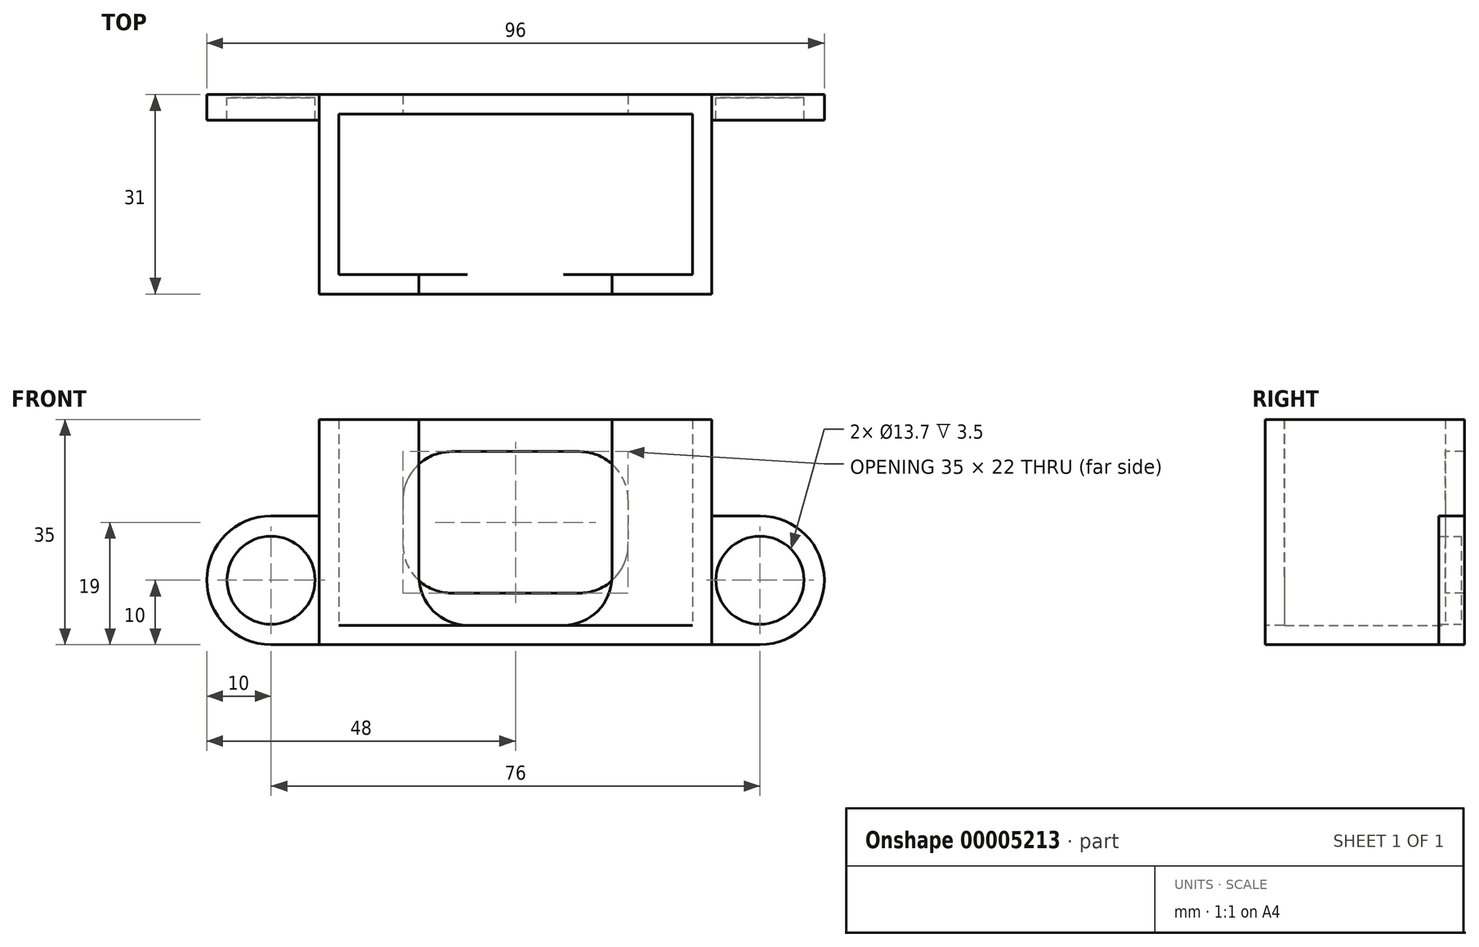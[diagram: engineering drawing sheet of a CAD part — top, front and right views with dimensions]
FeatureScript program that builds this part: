
annotation { "Feature Type Name" : "Feature", "Feature Type Description" : "" }
export const myFeature = defineFeature(function(context is Context, id is Id, definition is map)
    precondition{}
    {
        {
            var Q0;
            Q0=qCreatedBy(makeId("Top.planeOp"),FACE);
            var sketch = newSketch(context, id + "F0", { "sketchPlane" : qUnion([Q0])});
            skLineSegment(sketch, "E0.bottom", {"start": v(30.5, 15.5) * mm, "end": v(-30.5, 15.5) * mm});
            skLineSegment(sketch, "E0.top", {"start": v(30.5, -15.5) * mm, "end": v(-30.5, -15.5) * mm});
            skLineSegment(sketch, "E0.left", {"start": v(30.5, 15.5) * mm, "end": v(30.5, -15.5) * mm});
            skLineSegment(sketch, "E0.right", {"start": v(-30.5, 15.5) * mm, "end": v(-30.5, -15.5) * mm});
            skPoint(sketch, "E0.middle", {"position": v(0, 0) * mm});
            skLineSegment(sketch, "E1.bottom", {"start": v(27.5, 12.5) * mm, "end": v(-27.5, 12.5) * mm});
            skLineSegment(sketch, "E1.top", {"start": v(27.5, -12.5) * mm, "end": v(-27.5, -12.5) * mm});
            skLineSegment(sketch, "E1.left", {"start": v(27.5, 12.5) * mm, "end": v(27.5, -12.5) * mm});
            skLineSegment(sketch, "E1.right", {"start": v(-27.5, 12.5) * mm, "end": v(-27.5, -12.5) * mm});
            skSolve(sketch);
        }
        {
            var Q0;
            Q0 = qSketchRegion(id + "F0", true);
            extrude(context, id + "F1", {"entities" : qUnion([Q0]), "depth" : 35 * mm, "offsetDistance" : 25 * mm});
        }
        {
            var Q0;
            Q0=makeQuery(id+"F1.opExtrude","CAP_FACE",FACE,{"disambiguationData":[OSD([sQuery(id+"F0.wireOp",EDGE,"E0.bottom"),sQuery(id+"F0.wireOp",EDGE,"E0.top"),sQuery(id+"F0.wireOp",EDGE,"E0.left"),sQuery(id+"F0.wireOp",EDGE,"E0.right"),sQuery(id+"F0.wireOp",EDGE,"E1.bottom"),sQuery(id+"F0.wireOp",EDGE,"E1.top"),sQuery(id+"F0.wireOp",EDGE,"E1.left"),sQuery(id+"F0.wireOp",EDGE,"E1.right")])],"isStart":false});
            var sketch = newSketch(context, id + "F2", { "sketchPlane" : qUnion([Q0])});
            skLineSegment(sketch, "E2", {"start": v(0, -12.5) * mm, "end": v(0, -15.5) * mm, "construction": true});
            skLineSegment(sketch, "E3.bottom", {"start": v(15, -12.5) * mm, "end": v(-15, -12.5) * mm});
            skLineSegment(sketch, "E3.top", {"start": v(15, -15.5) * mm, "end": v(-15, -15.5) * mm});
            skLineSegment(sketch, "E3.left", {"start": v(15, -12.5) * mm, "end": v(15, -15.5) * mm});
            skLineSegment(sketch, "E3.right", {"start": v(-15, -12.5) * mm, "end": v(-15, -15.5) * mm});
            skPoint(sketch, "E3.middle", {"position": v(0, -14) * mm});
            skSolve(sketch);
        }
        {
            var Q0;
            Q0 = qSketchRegion(id + "F2", true);
            extrude(context, id + "F3", {"entities" : qUnion([Q0]), "operationType" : NewBodyOperationType.REMOVE, "endBound" : BoundingType.THROUGH_ALL, "oppositeDirection" : true, "depth" : 25 * mm, "offsetDistance" : 25 * mm});
        }
        {
            var Q0;
            Q0=makeQuery(id+"F1.opExtrude","CAP_FACE",FACE,{"disambiguationData":[OSD([sQuery(id+"F0.wireOp",EDGE,"E0.bottom"),sQuery(id+"F0.wireOp",EDGE,"E0.top"),sQuery(id+"F0.wireOp",EDGE,"E0.left"),sQuery(id+"F0.wireOp",EDGE,"E0.right"),sQuery(id+"F0.wireOp",EDGE,"E1.bottom"),sQuery(id+"F0.wireOp",EDGE,"E1.top"),sQuery(id+"F0.wireOp",EDGE,"E1.left"),sQuery(id+"F0.wireOp",EDGE,"E1.right")])],"isStart":true});
            var sketch = newSketch(context, id + "F4", { "sketchPlane" : qUnion([Q0])});
            skLineSegment(sketch, "E4.bottom", {"start": v(30.5, 15.5) * mm, "end": v(-30.5, 15.5) * mm});
            skLineSegment(sketch, "E4.top", {"start": v(30.5, -15.5) * mm, "end": v(-30.5, -15.5) * mm});
            skLineSegment(sketch, "E4.left", {"start": v(30.5, 15.5) * mm, "end": v(30.5, -15.5) * mm});
            skLineSegment(sketch, "E4.right", {"start": v(-30.5, 15.5) * mm, "end": v(-30.5, -15.5) * mm});
            skPoint(sketch, "E4.middle", {"position": v(0, 0) * mm});
            skSolve(sketch);
        }
        {
            var Q0;
            Q0 = qSketchRegion(id + "F4", true);
            extrude(context, id + "F5", {"entities" : qUnion([Q0]), "operationType" : NewBodyOperationType.ADD, "oppositeDirection" : true, "depth" : 3 * mm, "offsetDistance" : 25 * mm});
        }
        {
            var Q0;
            Q0=makeQuery(id+"F1.opExtrude","SWEPT_FACE",FACE,{"disambiguationData":[OSD([sQuery(id+"F0.wireOp",EDGE,"E0.bottom")])]});
            var sketch = newSketch(context, id + "F6", { "sketchPlane" : qUnion([Q0])});
            skCircle(sketch, "E5", {"center": v(-38, 10) * mm, "radius": 6.85 * mm});
            skLineSegment(sketch, "E6", {"start": v(0, 35) * mm, "end": v(0, 0) * mm, "construction": true});
            skArc(sketch, "E7", {"start": v(-38, 20) * mm, "mid": v(-48, 10) * mm, "end": v(-38, 0) * mm});
            skLineSegment(sketch, "E8", {"start": v(-38, 20) * mm, "end": v(-30.5, 20) * mm});
            skLineSegment(sketch, "E9", {"start": v(-30.5, 20) * mm, "end": v(-30.5, 0) * mm});
            skLineSegment(sketch, "E10", {"start": v(-30.5, 0) * mm, "end": v(-38, 0) * mm});
            skLineSegment(sketch, "E11.MirrorCS", {"start": v(30.5, 0) * mm, "end": v(38, 0) * mm});
            skCircle(sketch, "E12.MirrorC", {"center": v(38, 10) * mm, "radius": 6.85 * mm});
            skLineSegment(sketch, "E13.MirrorCS", {"start": v(30.5, 20) * mm, "end": v(30.5, 0) * mm});
            skLineSegment(sketch, "E14.MirrorCS", {"start": v(38, 20) * mm, "end": v(30.5, 20) * mm});
            skArc(sketch, "E15.MirrorCS", {"start": v(38, 20) * mm, "mid": v(48, 10) * mm, "end": v(38, 0) * mm});
            skSolve(sketch);
        }
        {
            var Q0;
            Q0 = qSketchRegion(id + "F6", true);
            extrude(context, id + "F7", {"entities" : qUnion([Q0]), "operationType" : NewBodyOperationType.ADD, "oppositeDirection" : true, "depth" : 4 * mm, "offsetDistance" : 25 * mm});
        }
        {
            var Q0;
            Q0=makeQuery(id+"F7.boolean.opBoolean","MERGE",FACE,{"derivedFrom":[makeQuery(id+"F1.opExtrude","SWEPT_FACE",FACE,{"disambiguationData":[OSD([sQuery(id+"F0.wireOp",EDGE,"E0.bottom")])]}),makeQuery(id+"F7.opExtrude","CAP_FACE",FACE,{"disambiguationData":[OSD([sQuery(id+"F6.wireOp",EDGE,"E5"),sQuery(id+"F6.wireOp",EDGE,"E7"),sQuery(id+"F6.wireOp",EDGE,"E8"),sQuery(id+"F6.wireOp",EDGE,"E9"),sQuery(id+"F6.wireOp",EDGE,"E10")])],"isStart":true}),makeQuery(id+"F7.opExtrude","CAP_FACE",FACE,{"disambiguationData":[OSD([sQuery(id+"F6.wireOp",EDGE,"E11.MirrorCS"),sQuery(id+"F6.wireOp",EDGE,"E12.MirrorC"),sQuery(id+"F6.wireOp",EDGE,"E13.MirrorCS"),sQuery(id+"F6.wireOp",EDGE,"E14.MirrorCS"),sQuery(id+"F6.wireOp",EDGE,"E15.MirrorCS")])],"isStart":true})]});
            var sketch = newSketch(context, id + "F8", { "sketchPlane" : qUnion([Q0])});
            skCircle(sketch, "E16.0", {"center": v(-38, 10) * mm, "radius": 6.85 * mm});
            skCircle(sketch, "E16.1", {"center": v(38, 10) * mm, "radius": 6.85 * mm});
            skSolve(sketch);
        }
        {
            var Q0;
            Q0 = qSketchRegion(id + "F8", true);
            extrude(context, id + "F9", {"entities" : qUnion([Q0]), "operationType" : NewBodyOperationType.ADD, "oppositeDirection" : true, "depth" : 0.5 * mm, "offsetDistance" : 25 * mm});
        }
        {
            var Q0;
            Q0=makeQuery(id+"F1.opExtrude","SWEPT_FACE",FACE,{"disambiguationData":[OSD([sQuery(id+"F0.wireOp",EDGE,"E1.bottom")])]});
            var sketch = newSketch(context, id + "F10", { "sketchPlane" : qUnion([Q0])});
            skLineSegment(sketch, "E17", {"start": v(-27.5, 19) * mm, "end": v(27.5, 19) * mm, "construction": true});
            skLineSegment(sketch, "E18.bottom", {"start": v(17.5, 30) * mm, "end": v(-17.5, 30) * mm});
            skLineSegment(sketch, "E18.top", {"start": v(17.5, 8) * mm, "end": v(-17.5, 8) * mm});
            skLineSegment(sketch, "E18.left", {"start": v(17.5, 30) * mm, "end": v(17.5, 8) * mm});
            skLineSegment(sketch, "E18.right", {"start": v(-17.5, 30) * mm, "end": v(-17.5, 8) * mm});
            skPoint(sketch, "E18.middle", {"position": v(0, 19) * mm});
            skSolve(sketch);
        }
        {
            var Q0;
            Q0 = qSketchRegion(id + "F10", true);
            extrude(context, id + "F11", {"entities" : qUnion([Q0]), "operationType" : NewBodyOperationType.REMOVE, "oppositeDirection" : true, "depth" : 25 * mm, "offsetDistance" : 25 * mm});
        }
        {
            var Q0;
            Q0=makeQuery(id+"F7.opExtrude","SWEPT_EDGE",EDGE,{"disambiguationData":[OSD([sQuery(id+"F0.wireOp",EDGE,"E0.bottom"),sQuery(id+"F0.wireOp",EDGE,"E0.left"),sQuery(id+"F6.wireOp",EDGE,"E8"),sQuery(id+"F6.wireOp",EDGE,"E9")])]});
            var Q1;
            Q1=makeQuery(id+"F7.opExtrude","SWEPT_EDGE",EDGE,{"disambiguationData":[OSD([sQuery(id+"F0.wireOp",EDGE,"E0.bottom"),sQuery(id+"F0.wireOp",EDGE,"E0.right"),sQuery(id+"F6.wireOp",EDGE,"E13.MirrorCS"),sQuery(id+"F6.wireOp",EDGE,"E14.MirrorCS")])]});
            var Q2;
            Q2=makeQuery(id+"F3.boolean.opBoolean","COPY",EDGE,{"derivedFrom":makeQuery(id+"F3.opExtrude","CAP_EDGE",EDGE,{"disambiguationData":[OSD([sQuery(id+"F2.wireOp",EDGE,"E3.right")])],"isStart":true})});
            var Q3;
            Q3=makeQuery(id+"F3.boolean.opBoolean","COPY",EDGE,{"derivedFrom":makeQuery(id+"F3.opExtrude","CAP_EDGE",EDGE,{"disambiguationData":[OSD([sQuery(id+"F2.wireOp",EDGE,"E3.left")])],"isStart":true})});
            var Q4;
            Q4=makeQuery(id+"F5.boolean.opBoolean","INTERSECT",EDGE,{"derivedFrom":[makeQuery(id+"F3.boolean.opBoolean","COPY",FACE,{"derivedFrom":makeQuery(id+"F3.opExtrude","SWEPT_FACE",FACE,{"disambiguationData":[OSD([sQuery(id+"F2.wireOp",EDGE,"E3.right")])]})}),makeQuery(id+"F5.opExtrude","CAP_FACE",FACE,{"disambiguationData":[OSD([sQuery(id+"F4.wireOp",EDGE,"E4.bottom"),sQuery(id+"F4.wireOp",EDGE,"E4.top"),sQuery(id+"F4.wireOp",EDGE,"E4.left"),sQuery(id+"F4.wireOp",EDGE,"E4.right")])],"isStart":false})]});
            var Q5;
            Q5=makeQuery(id+"F5.boolean.opBoolean","INTERSECT",EDGE,{"derivedFrom":[makeQuery(id+"F3.boolean.opBoolean","COPY",FACE,{"derivedFrom":makeQuery(id+"F3.opExtrude","SWEPT_FACE",FACE,{"disambiguationData":[OSD([sQuery(id+"F2.wireOp",EDGE,"E3.left")])]})}),makeQuery(id+"F5.opExtrude","CAP_FACE",FACE,{"disambiguationData":[OSD([sQuery(id+"F4.wireOp",EDGE,"E4.bottom"),sQuery(id+"F4.wireOp",EDGE,"E4.top"),sQuery(id+"F4.wireOp",EDGE,"E4.left"),sQuery(id+"F4.wireOp",EDGE,"E4.right")])],"isStart":false})]});
            var Q6;
            Q6=makeQuery(id+"F11.boolean.opBoolean","COPY",EDGE,{"derivedFrom":makeQuery(id+"F11.opExtrude","SWEPT_EDGE",EDGE,{"disambiguationData":[OSD([sQuery(id+"F10.wireOp",EDGE,"E18.bottom"),sQuery(id+"F10.wireOp",EDGE,"E18.left")])]})});
            var Q7;
            Q7=makeQuery(id+"F11.boolean.opBoolean","COPY",EDGE,{"derivedFrom":makeQuery(id+"F11.opExtrude","SWEPT_EDGE",EDGE,{"disambiguationData":[OSD([sQuery(id+"F10.wireOp",EDGE,"E18.bottom"),sQuery(id+"F10.wireOp",EDGE,"E18.right")])]})});
            var Q8;
            Q8=makeQuery(id+"F11.boolean.opBoolean","COPY",EDGE,{"derivedFrom":makeQuery(id+"F11.opExtrude","SWEPT_EDGE",EDGE,{"disambiguationData":[OSD([sQuery(id+"F10.wireOp",EDGE,"E18.top"),sQuery(id+"F10.wireOp",EDGE,"E18.right")])]})});
            var Q9;
            Q9=makeQuery(id+"F11.boolean.opBoolean","COPY",EDGE,{"derivedFrom":makeQuery(id+"F11.opExtrude","SWEPT_EDGE",EDGE,{"disambiguationData":[OSD([sQuery(id+"F10.wireOp",EDGE,"E18.top"),sQuery(id+"F10.wireOp",EDGE,"E18.left")])]})});
            var Q10;
            Q10=makeQuery(id+"F7.opExtrude","CAP_EDGE",EDGE,{"disambiguationData":[OSD([sQuery(id+"F6.wireOp",EDGE,"E13.MirrorCS")])],"isStart":false});
            var Q11;
            Q11=makeQuery(id+"F7.opExtrude","CAP_EDGE",EDGE,{"disambiguationData":[OSD([sQuery(id+"F6.wireOp",EDGE,"E9")])],"isStart":false});
            fillet(context, id + "F12", {"entities" : qUnion([Q0, Q1, Q2, Q3, Q4, Q5, Q6, Q7, Q8, Q9, Q10, Q11]), "tangentPropagation" : true, "radius" : 7.55 * mm, "defaultsChanged" : false, "vertexSettings" : [], "allowEdgeOverflow" : false});
        }
    });
